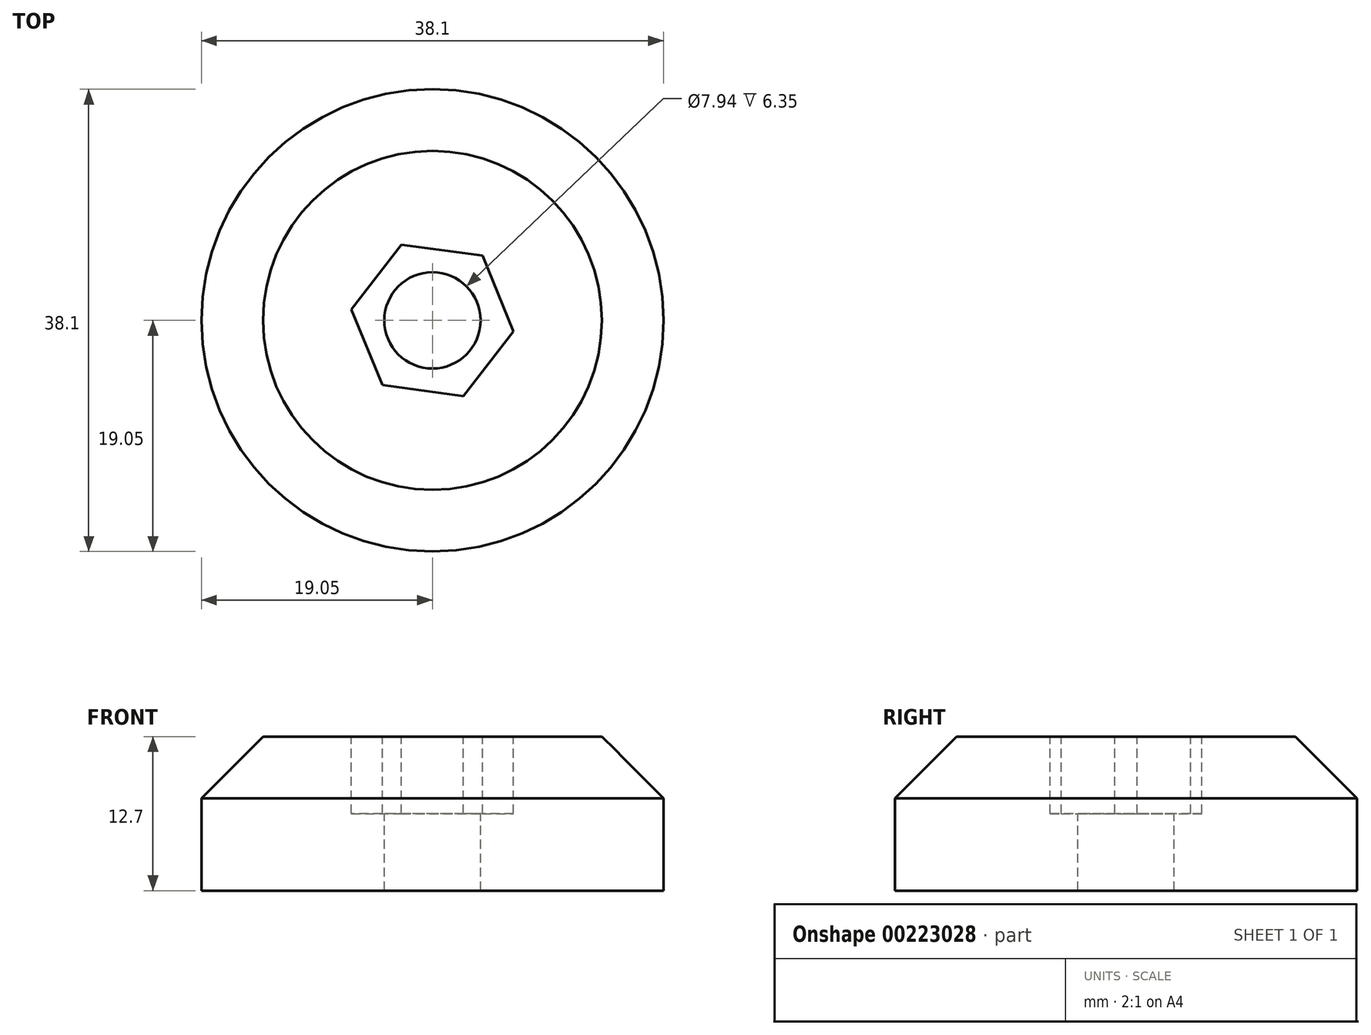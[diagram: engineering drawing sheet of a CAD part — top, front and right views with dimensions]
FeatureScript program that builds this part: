
annotation { "Feature Type Name" : "Feature", "Feature Type Description" : "" }
export const myFeature = defineFeature(function(context is Context, id is Id, definition is map)
    precondition{}
    {
        {
            var Q0;
            Q0=qCreatedBy(makeId("Top.planeOp"),FACE);
            var sketch = newSketch(context, id + "F0", { "sketchPlane" : qUnion([Q0])});
            skCircle(sketch, "E0", {"center": v(0, 0) * mm, "radius": 19.05 * mm});
            skSolve(sketch);
        }
        {
            var Q0;
            Q0=makeQuery(id+"F0.imprint","IMPRINT",FACE,{"disambiguationData":[TD([[makeQuery(id+"F0.imprint","IMPRINT",EDGE,{"derivedFrom":sQuery(id+"F0.wireOp",EDGE,"E0")}),1.0]])]});
            extrude(context, id + "F1", {"entities" : qUnion([Q0]), "depth" : 12.7 * mm});
        }
        {
            var Q0;
            Q0=makeQuery(id+"F1.opExtrude","CAP_FACE",FACE,{"disambiguationData":[OSD([sQuery(id+"F0.wireOp",EDGE,"E0")])],"isStart":false});
            var sketch = newSketch(context, id + "F2", { "sketchPlane" : qUnion([Q0])});
            skCircle(sketch, "E1.cCircle", {"center": v(0, 0) * mm, "radius": 5.84 * mm, "construction": true});
            skLineSegment(sketch, "E1.0", {"start": v(4.13, 5.33) * mm, "end": v(6.68, -0.9) * mm});
            skLineSegment(sketch, "E1.1", {"start": v(6.68, -0.9) * mm, "end": v(2.56, -6.24) * mm});
            skLineSegment(sketch, "E1.2", {"start": v(2.56, -6.24) * mm, "end": v(-4.13, -5.33) * mm});
            skLineSegment(sketch, "E1.3", {"start": v(-4.13, -5.33) * mm, "end": v(-6.68, 0.9) * mm});
            skLineSegment(sketch, "E1.4", {"start": v(-6.68, 0.9) * mm, "end": v(-2.56, 6.24) * mm});
            skLineSegment(sketch, "E1.5", {"start": v(-2.56, 6.24) * mm, "end": v(4.13, 5.33) * mm});
            skPoint(sketch, "E1.0.midPoint", {"position": v(5.4, 2.21) * mm});
            skSolve(sketch);
        }
        {
            var Q0;
            Q0 = qSketchRegion(id + "F2", true);
            extrude(context, id + "F3", {"entities" : qUnion([Q0]), "operationType" : NewBodyOperationType.REMOVE, "oppositeDirection" : true, "depth" : 6.35 * mm});
        }
        {
            var Q0;
            Q0=makeQuery(id+"F3.boolean.opBoolean","COPY",FACE,{"derivedFrom":makeQuery(id+"F3.opExtrude","CAP_FACE",FACE,{"disambiguationData":[OSD([sQuery(id+"F2.wireOp",EDGE,"E1.0"),sQuery(id+"F2.wireOp",EDGE,"E1.1"),sQuery(id+"F2.wireOp",EDGE,"E1.2"),sQuery(id+"F2.wireOp",EDGE,"E1.3"),sQuery(id+"F2.wireOp",EDGE,"E1.4"),sQuery(id+"F2.wireOp",EDGE,"E1.5")])],"isStart":false})});
            var sketch = newSketch(context, id + "F4", { "sketchPlane" : qUnion([Q0])});
            skCircle(sketch, "E2", {"center": v(0, 0) * mm, "radius": 3.97 * mm});
            skSolve(sketch);
        }
        {
            var Q0;
            Q0 = qSketchRegion(id + "F4", true);
            extrude(context, id + "F5", {"entities" : qUnion([Q0]), "operationType" : NewBodyOperationType.REMOVE, "endBound" : BoundingType.THROUGH_ALL, "oppositeDirection" : true, "depth" : 25.4 * mm});
        }
        {
            var Q0;
            Q0=makeQuery(id+"F1.opExtrude","CAP_EDGE",EDGE,{"disambiguationData":[OSD([sQuery(id+"F0.wireOp",EDGE,"E0")])],"isStart":false});
            chamfer(context, id + "F6", {"entities" : qUnion([Q0]), "width" : 5.08 * mm, "tangentPropagation" : true});
        }
    });
